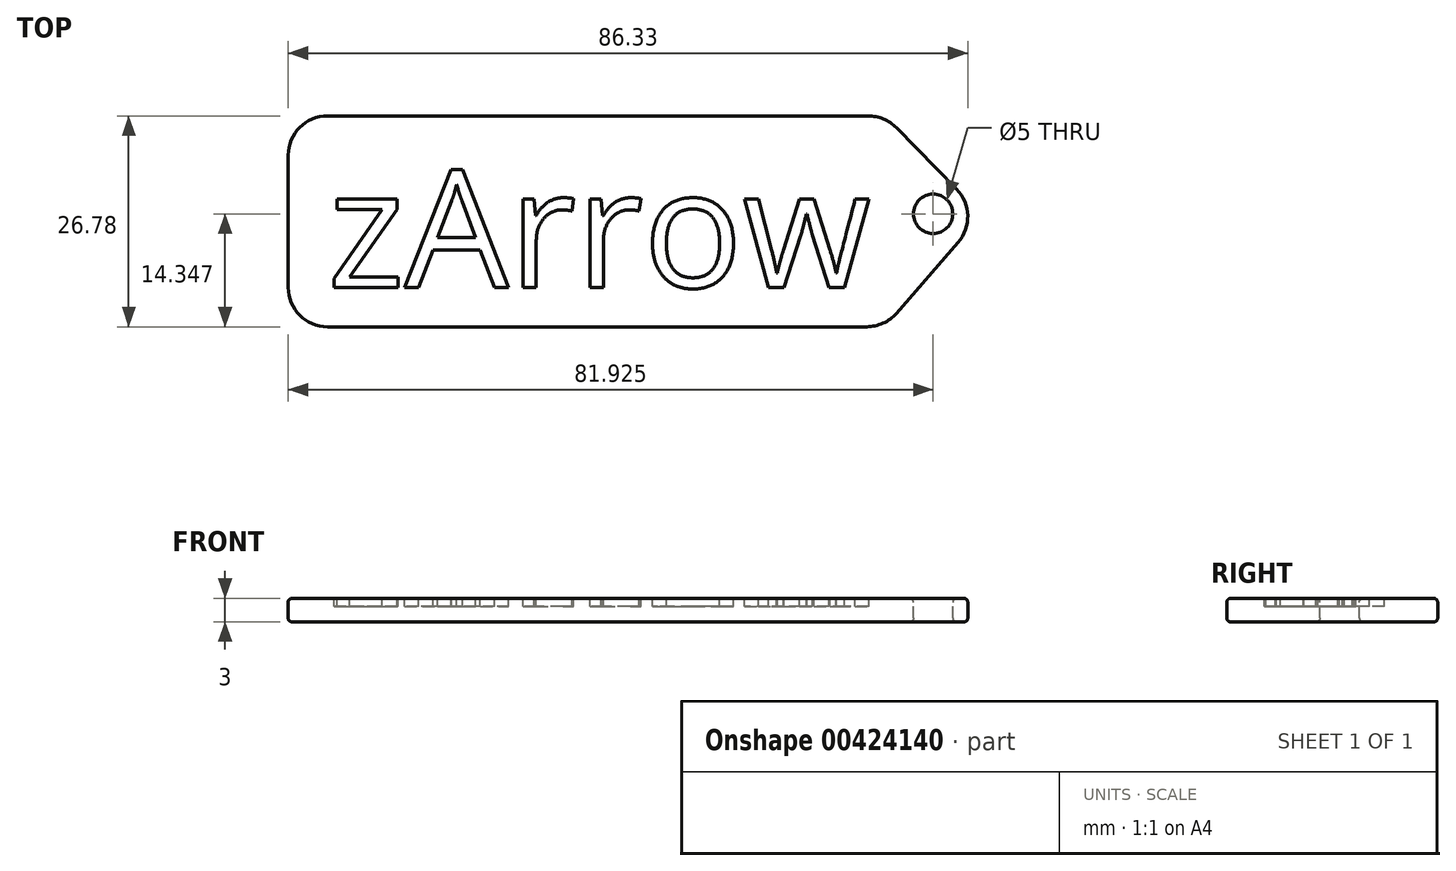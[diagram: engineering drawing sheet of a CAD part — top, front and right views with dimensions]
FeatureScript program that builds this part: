
annotation { "Feature Type Name" : "Feature", "Feature Type Description" : "" }
export const myFeature = defineFeature(function(context is Context, id is Id, definition is map)
    precondition{}
    {
        {
            var Q0;
            Q0=qCreatedBy(makeId("Top.planeOp"),FACE);
            var sketch = newSketch(context, id + "F0", { "sketchPlane" : qUnion([Q0])});
            skLineSegment(sketch, "E0.bottom", {"start": v(-38, 16.48) * mm, "end": v(37.77, 16.48) * mm});
            skLineSegment(sketch, "E0.top", {"start": v(-38, -10.3) * mm, "end": v(37.77, -10.3) * mm});
            skLineSegment(sketch, "E0.left", {"start": v(-38, 16.48) * mm, "end": v(-38, -10.3) * mm});
            skLineSegment(sketch, "E1", {"start": v(37.77, 16.48) * mm, "end": v(50.13, 3.9) * mm});
            skLineSegment(sketch, "E2", {"start": v(50.13, 3.9) * mm, "end": v(37.77, -10.3) * mm});
            skSolve(sketch);
        }
        {
            var Q0;
            Q0=makeQuery(id+"F0.imprint","IMPRINT",FACE,{"disambiguationData":[TD([[makeQuery(id+"F0.imprint","IMPRINT",EDGE,{"derivedFrom":sQuery(id+"F0.wireOp",EDGE,"E0.bottom")}),-1.0]])]});
            extrude(context, id + "F1", {"entities" : qUnion([Q0]), "depth" : 3 * mm});
        }
        {
            var Q0;
            Q0=makeQuery(id+"F1.opExtrude","SWEPT_EDGE",EDGE,{"disambiguationData":[OSD([sQuery(id+"F0.wireOp",EDGE,"E0.top"),sQuery(id+"F0.wireOp",EDGE,"E2")])]});
            var Q1;
            Q1=makeQuery(id+"F1.opExtrude","SWEPT_EDGE",EDGE,{"disambiguationData":[OSD([sQuery(id+"F0.wireOp",EDGE,"E1"),sQuery(id+"F0.wireOp",EDGE,"E2")])]});
            var Q2;
            Q2=makeQuery(id+"F1.opExtrude","SWEPT_EDGE",EDGE,{"disambiguationData":[OSD([sQuery(id+"F0.wireOp",EDGE,"E0.bottom"),sQuery(id+"F0.wireOp",EDGE,"E1")])]});
            var Q3;
            Q3=makeQuery(id+"F1.opExtrude","SWEPT_EDGE",EDGE,{"disambiguationData":[OSD([sQuery(id+"F0.wireOp",EDGE,"E0.bottom"),sQuery(id+"F0.wireOp",EDGE,"E0.left")])]});
            var Q4;
            Q4=makeQuery(id+"F1.opExtrude","SWEPT_EDGE",EDGE,{"disambiguationData":[OSD([sQuery(id+"F0.wireOp",EDGE,"E0.top"),sQuery(id+"F0.wireOp",EDGE,"E0.left")])]});
            fillet(context, id + "F2", {"entities" : qUnion([Q0, Q1, Q2, Q3, Q4]), "radius" : 5 * mm, "tangentPropagation" : true, "allowEdgeOverflow" : false});
        }
        {
            var Q0;
            Q0=makeQuery(id+"F1.opExtrude","CAP_FACE",FACE,{"disambiguationData":[OSD([sQuery(id+"F0.wireOp",EDGE,"E0.bottom"),sQuery(id+"F0.wireOp",EDGE,"E0.top"),sQuery(id+"F0.wireOp",EDGE,"E0.left"),sQuery(id+"F0.wireOp",EDGE,"E1"),sQuery(id+"F0.wireOp",EDGE,"E2")])],"isStart":false});
            var sketch = newSketch(context, id + "F3", { "sketchPlane" : qUnion([Q0])});
            skCircle(sketch, "E3", {"center": v(43.93, 4.05) * mm, "radius": 1.7 * mm});
            skSolve(sketch);
        }
        {
            var Q0;
            Q0=sQuery(id+"F3.wireOp",VERTEX,"E3.center");
            var Q1;
            Q1=makeQuery(id+"F1.opExtrude","SWEPT_BODY",BODY,{"disambiguationData":[OSD([sQuery(id+"F0.wireOp",EDGE,"E0.bottom"),sQuery(id+"F0.wireOp",EDGE,"E0.top"),sQuery(id+"F0.wireOp",EDGE,"E0.left"),sQuery(id+"F0.wireOp",EDGE,"E1"),sQuery(id+"F0.wireOp",EDGE,"E2")])]});
            hole(context, id + "F4", {"style" : HoleStyle.SIMPLE, "endStyle" : HoleEndStyle.THROUGH, "holeDiameter" : 5 * mm, "isTappedThrough" : true, "tappedDepth" : 12 * mm, "tapClearance" : 3, "startFromSketch" : true, "locations" : qUnion([Q0]), "scope" : qUnion([Q1])});
        }
        {
            var Q0;
            Q0=makeQuery(id+"F1.opExtrude","CAP_FACE",FACE,{"disambiguationData":[OSD([sQuery(id+"F0.wireOp",EDGE,"E0.bottom"),sQuery(id+"F0.wireOp",EDGE,"E0.top"),sQuery(id+"F0.wireOp",EDGE,"E0.left"),sQuery(id+"F0.wireOp",EDGE,"E1"),sQuery(id+"F0.wireOp",EDGE,"E2")])],"isStart":false});
            fillet(context, id + "F5", {"entities" : qUnion([Q0]), "radius" : 0.5 * mm, "tangentPropagation" : true, "allowEdgeOverflow" : false});
        }
        {
            var Q0;
            Q0=makeQuery(id+"F1.opExtrude","CAP_FACE",FACE,{"disambiguationData":[OSD([sQuery(id+"F0.wireOp",EDGE,"E0.bottom"),sQuery(id+"F0.wireOp",EDGE,"E0.top"),sQuery(id+"F0.wireOp",EDGE,"E0.left"),sQuery(id+"F0.wireOp",EDGE,"E1"),sQuery(id+"F0.wireOp",EDGE,"E2")])],"isStart":true});
            fillet(context, id + "F6", {"entities" : qUnion([Q0]), "radius" : 0.5 * mm, "tangentPropagation" : true, "allowEdgeOverflow" : false});
        }
        {
            var Q0;
            Q0=makeQuery(id+"F1.opExtrude","CAP_FACE",FACE,{"disambiguationData":[OSD([sQuery(id+"F0.wireOp",EDGE,"E0.bottom"),sQuery(id+"F0.wireOp",EDGE,"E0.top"),sQuery(id+"F0.wireOp",EDGE,"E0.left"),sQuery(id+"F0.wireOp",EDGE,"E1"),sQuery(id+"F0.wireOp",EDGE,"E2")])],"isStart":false});
            var sketch = newSketch(context, id + "F7", { "sketchPlane" : qUnion([Q0])});
            skText(sketch, "E4", { "text": "zArrow", "fontName": "OpenSans-Regular.ttf"});
            const initialGuessF7  = {"E4": [-0.033, -0.0053, 1, 0, 0.01506]};
            skSetInitialGuess(sketch, initialGuessF7);
            skSolve(sketch);
        }
        {
            var Q0;
            Q0 = qSketchRegion(id + "F7", true);
            extrude(context, id + "F8", {"entities" : qUnion([Q0]), "operationType" : NewBodyOperationType.REMOVE, "oppositeDirection" : true, "depth" : 1 * mm});
        }
    });
